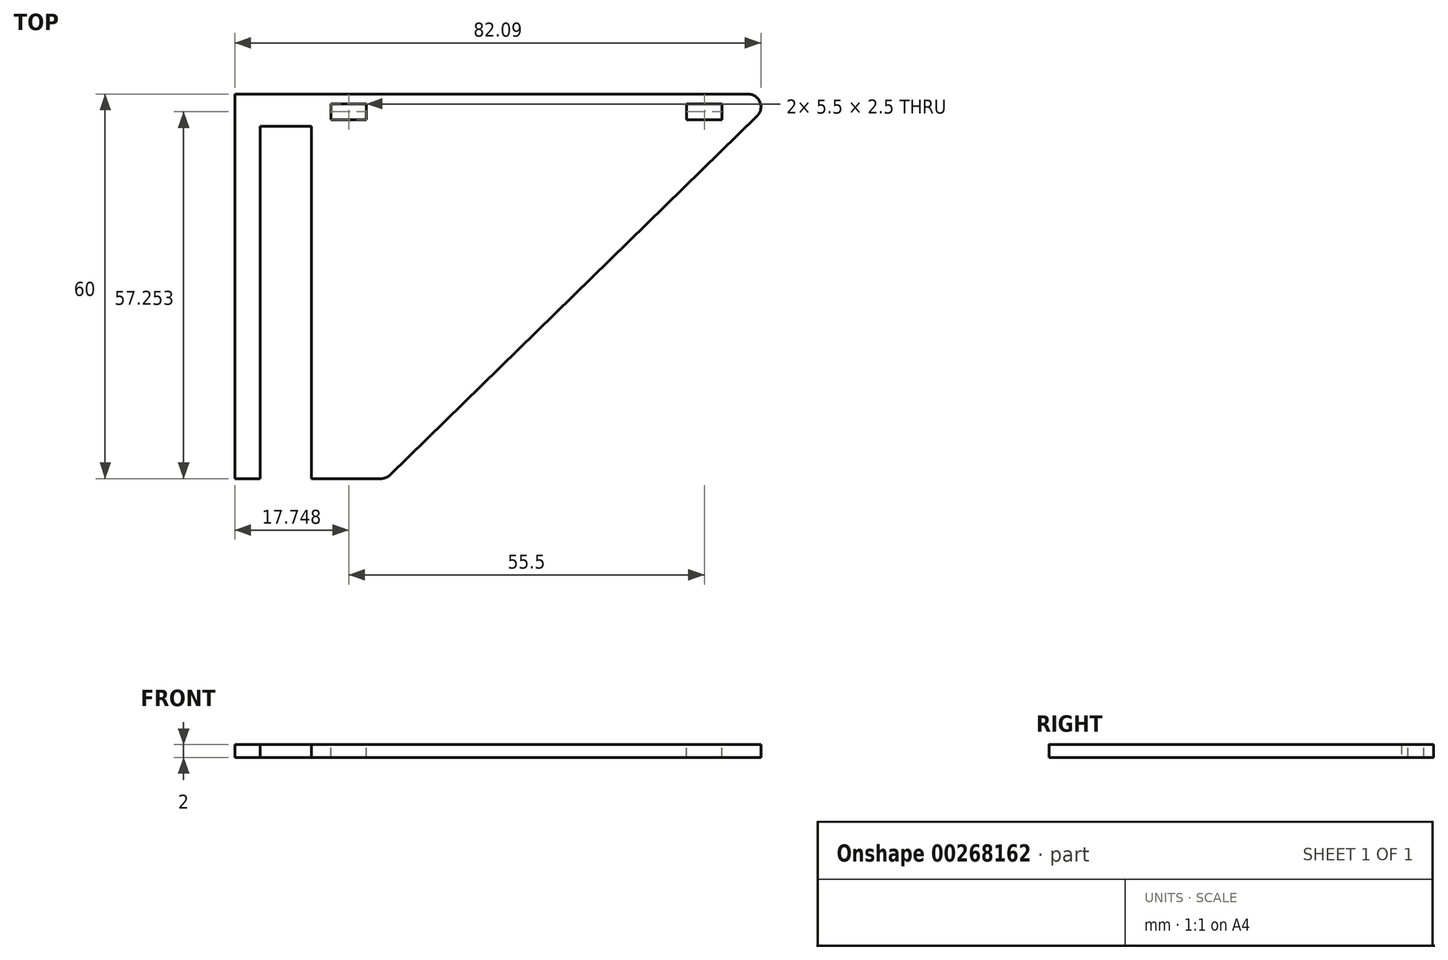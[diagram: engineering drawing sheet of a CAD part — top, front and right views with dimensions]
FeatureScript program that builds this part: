
annotation { "Feature Type Name" : "Feature", "Feature Type Description" : "" }
export const myFeature = defineFeature(function(context is Context, id is Id, definition is map)
    precondition{}
    {
        {
            var Q0;
            Q0=qCreatedBy(makeId("Top.planeOp"),FACE);
            var sketch = newSketch(context, id + "F0", { "sketchPlane" : qUnion([Q0])});
            skLineSegment(sketch, "E0", {"start": v(-67.52, 39.36) * mm, "end": v(-67.52, -20.64) * mm});
            skLineSegment(sketch, "E1", {"start": v(-67.52, -20.64) * mm, "end": v(-44.73, -20.64) * mm});
            skLineSegment(sketch, "E2", {"start": v(-43.33, -20.07) * mm, "end": v(13.97, 35.93) * mm});
            skLineSegment(sketch, "E3", {"start": v(12.57, 39.36) * mm, "end": v(-67.52, 39.36) * mm});
            skPoint(sketch, "E4.visualSharp", {"position": v(17.48, 39.36) * mm});
            skArc(sketch, "E4.filletArc", {"start": v(13.97, 35.93) * mm, "mid": v(14.42, 38.12) * mm, "end": v(12.57, 39.36) * mm});
            skPoint(sketch, "E5.visualSharp", {"position": v(-43.92, -20.64) * mm});
            skArc(sketch, "E5.filletArc", {"start": v(-44.73, -20.64) * mm, "mid": v(-43.98, -20.49) * mm, "end": v(-43.33, -20.07) * mm});
            skLineSegment(sketch, "E6.bottom", {"start": v(-63.57, -20.64) * mm, "end": v(-55.57, -20.64) * mm});
            skLineSegment(sketch, "E6.top", {"start": v(-63.57, 34.36) * mm, "end": v(-55.57, 34.36) * mm});
            skLineSegment(sketch, "E6.left", {"start": v(-63.57, -20.64) * mm, "end": v(-63.57, 34.36) * mm});
            skLineSegment(sketch, "E6.right", {"start": v(-55.57, -20.64) * mm, "end": v(-55.57, 34.36) * mm});
            skSolve(sketch);
        }
        {
            var Q0;
            {var subQ5=sQuery(id+"F0.wireOp",EDGE,"E0");Q0=makeQuery(id+"F0.imprint","IMPRINT",FACE,{"disambiguationData":[TD([[makeQuery(id+"F0.imprint","IMPRINT",EDGE,{"derivedFrom":subQ5}),1.0]])]});}
            extrude(context, id + "F1", {"entities" : qUnion([Q0]), "depth" : 2 * mm});
        }
        {
            var Q0;
            Q0=makeQuery(id+"F1.opExtrude","CAP_FACE",FACE,{"disambiguationData":[OSD([sQuery(id+"F0.wireOp",EDGE,"E0"),sQuery(id+"F0.wireOp",EDGE,"E1"),sQuery(id+"F0.wireOp",EDGE,"E2"),sQuery(id+"F0.wireOp",EDGE,"E3"),sQuery(id+"F0.wireOp",EDGE,"E4.filletArc"),sQuery(id+"F0.wireOp",EDGE,"E5.filletArc"),sQuery(id+"F0.wireOp",EDGE,"E6.top"),sQuery(id+"F0.wireOp",EDGE,"E6.left"),sQuery(id+"F0.wireOp",EDGE,"E6.right")])],"isStart":false});
            var sketch = newSketch(context, id + "F2", { "sketchPlane" : qUnion([Q0])});
            skLineSegment(sketch, "E7.bottom", {"start": v(-52.52, 37.86) * mm, "end": v(-47.02, 37.86) * mm});
            skLineSegment(sketch, "E7.top", {"start": v(-52.52, 35.36) * mm, "end": v(-47.02, 35.36) * mm});
            skLineSegment(sketch, "E7.left", {"start": v(-52.52, 37.86) * mm, "end": v(-52.52, 35.36) * mm});
            skLineSegment(sketch, "E7.right", {"start": v(-47.02, 37.86) * mm, "end": v(-47.02, 35.36) * mm});
            skLineSegment(sketch, "E8.bottom", {"start": v(8.48, 37.86) * mm, "end": v(2.98, 37.86) * mm});
            skLineSegment(sketch, "E8.top", {"start": v(8.48, 35.36) * mm, "end": v(2.98, 35.36) * mm});
            skLineSegment(sketch, "E8.left", {"start": v(8.48, 37.86) * mm, "end": v(8.48, 35.36) * mm});
            skLineSegment(sketch, "E8.right", {"start": v(2.98, 37.86) * mm, "end": v(2.98, 35.36) * mm});
            skSolve(sketch);
        }
        {
            var Q0;
            Q0 = qSketchRegion(id + "F2", true);
            extrude(context, id + "F3", {"entities" : qUnion([Q0]), "operationType" : NewBodyOperationType.REMOVE, "oppositeDirection" : true, "depth" : 25 * mm});
        }
    });
